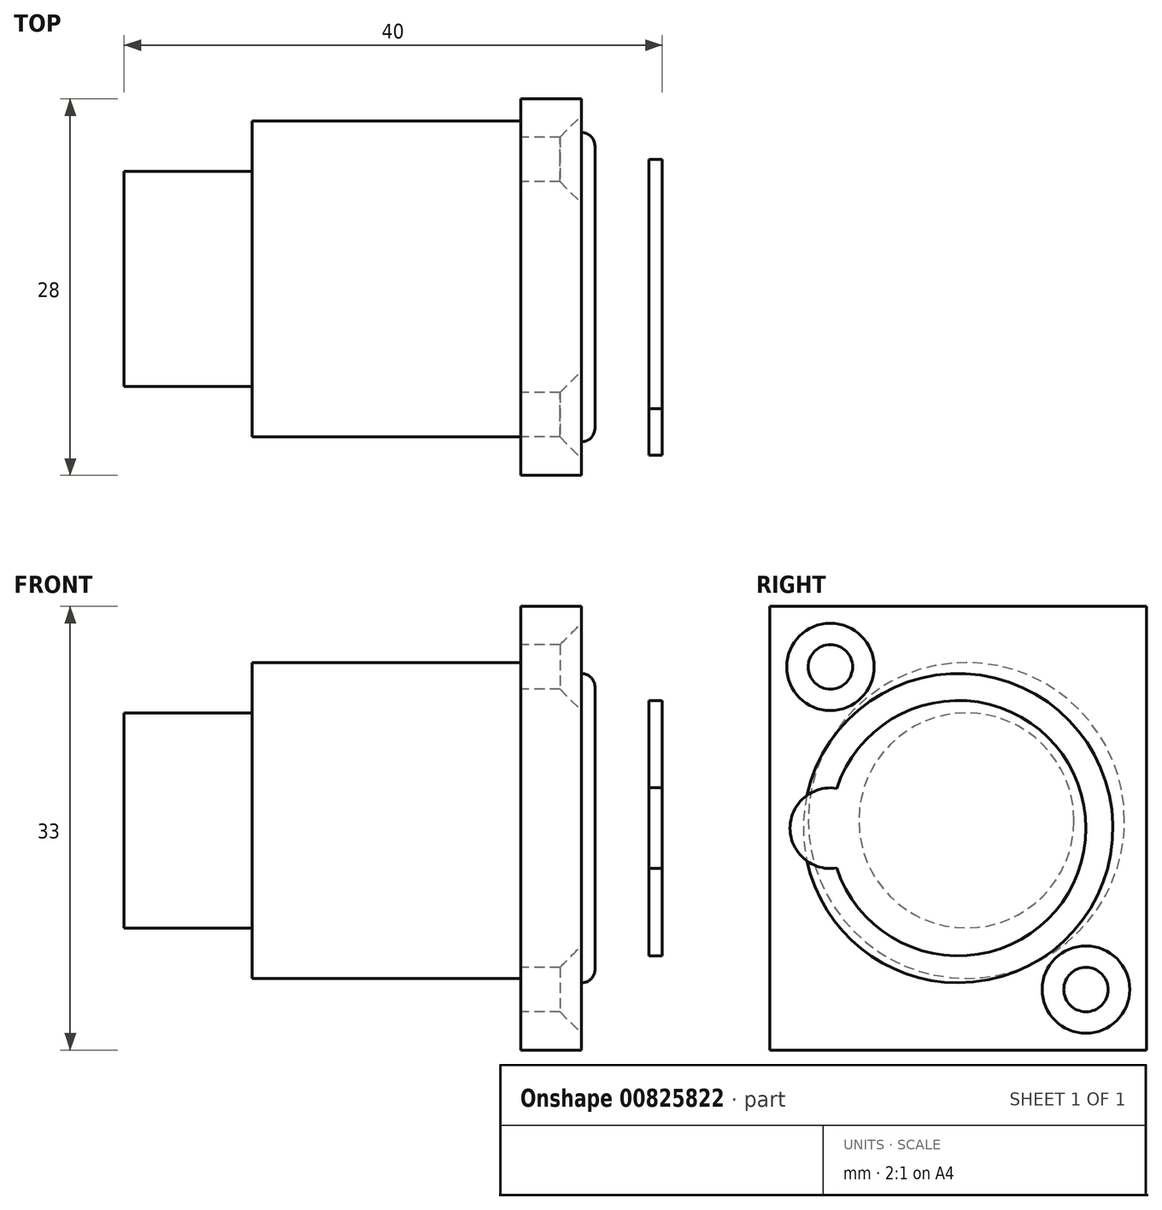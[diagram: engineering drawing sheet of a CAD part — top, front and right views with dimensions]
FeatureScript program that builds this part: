
annotation { "Feature Type Name" : "Feature", "Feature Type Description" : "" }
export const myFeature = defineFeature(function(context is Context, id is Id, definition is map)
    precondition{}
    {
        {
            var Q0;
            Q0=qCreatedBy(makeId("Right.planeOp"),FACE);
            var sketch = newSketch(context, id + "F0", { "sketchPlane" : qUnion([Q0])});
            skLineSegment(sketch, "E0.bottom", {"start": v(0, 0) * mm, "end": v(28, 0) * mm});
            skLineSegment(sketch, "E0.top", {"start": v(0, -33) * mm, "end": v(28, -33) * mm});
            skLineSegment(sketch, "E0.left", {"start": v(0, 0) * mm, "end": v(0, -33) * mm});
            skLineSegment(sketch, "E0.right", {"start": v(28, 0) * mm, "end": v(28, -33) * mm});
            skSolve(sketch);
        }
        {
            var Q0;
            Q0=makeQuery(id+"F0.imprint","IMPRINT",FACE,{"disambiguationData":[TD([[makeQuery(id+"F0.imprint","IMPRINT",EDGE,{"derivedFrom":sQuery(id+"F0.wireOp",EDGE,"E0.bottom")}),-1.0]])]});
            extrude(context, id + "F1", {"entities" : qUnion([Q0]), "depth" : 4.5 * mm, "offsetDistance" : 25 * mm});
        }
        {
            var Q0;
            Q0=makeQuery(id+"F1.opExtrude","CAP_FACE",FACE,{"disambiguationData":[OSD([sQuery(id+"F0.wireOp",EDGE,"E0.bottom"),sQuery(id+"F0.wireOp",EDGE,"E0.top"),sQuery(id+"F0.wireOp",EDGE,"E0.left"),sQuery(id+"F0.wireOp",EDGE,"E0.right")])],"isStart":true});
            var sketch = newSketch(context, id + "F2", { "sketchPlane" : qUnion([Q0])});
            skCircle(sketch, "E1", {"center": v(-14.61, -15.92) * mm, "radius": 11.75 * mm});
            skSolve(sketch);
        }
        {
            var Q0;
            Q0=makeQuery(id+"F2.imprint","IMPRINT",FACE,{"disambiguationData":[TD([[makeQuery(id+"F2.imprint","IMPRINT",EDGE,{"derivedFrom":sQuery(id+"F2.wireOp",EDGE,"E1")}),1.0]])]});
            extrude(context, id + "F3", {"entities" : qUnion([Q0]), "depth" : 20 * mm, "offsetDistance" : 25 * mm});
        }
        {
            var Q0;
            Q0=makeQuery(id+"F3.opExtrude","CAP_FACE",FACE,{"disambiguationData":[OSD([sQuery(id+"F2.wireOp",EDGE,"E1")])],"isStart":false});
            var sketch = newSketch(context, id + "F4", { "sketchPlane" : qUnion([Q0])});
            skCircle(sketch, "E2", {"center": v(-14.61, -15.92) * mm, "radius": 8 * mm});
            skSolve(sketch);
        }
        {
            var Q0;
            Q0=makeQuery(id+"F4.imprint","IMPRINT",FACE,{"disambiguationData":[TD([[makeQuery(id+"F4.imprint","IMPRINT",EDGE,{"derivedFrom":sQuery(id+"F4.wireOp",EDGE,"E2")}),1.0]])]});
            extrude(context, id + "F5", {"entities" : qUnion([Q0]), "operationType" : NewBodyOperationType.ADD, "depth" : 9.5 * mm, "offsetDistance" : 25 * mm});
        }
        {
            var Q0;
            Q0=makeQuery(id+"F1.opExtrude","CAP_FACE",FACE,{"disambiguationData":[OSD([sQuery(id+"F0.wireOp",EDGE,"E0.bottom"),sQuery(id+"F0.wireOp",EDGE,"E0.top"),sQuery(id+"F0.wireOp",EDGE,"E0.left"),sQuery(id+"F0.wireOp",EDGE,"E0.right")])],"isStart":false});
            var sketch = newSketch(context, id + "F6", { "sketchPlane" : qUnion([Q0])});
            skCircle(sketch, "E3", {"center": v(14, -16.5) * mm, "radius": 11.5 * mm});
            skPoint(sketch, "E4", {"position": v(14, 0) * mm});
            skPoint(sketch, "E5", {"position": v(0, -16.5) * mm});
            skSolve(sketch);
        }
        {
            var Q0;
            Q0=makeQuery(id+"F6.imprint","IMPRINT",FACE,{"disambiguationData":[TD([[makeQuery(id+"F6.imprint","IMPRINT",EDGE,{"derivedFrom":sQuery(id+"F6.wireOp",EDGE,"E3")}),1.0]])]});
            extrude(context, id + "F7", {"entities" : qUnion([Q0]), "operationType" : NewBodyOperationType.ADD, "depth" : 1 * mm, "offsetDistance" : 25 * mm});
        }
        {
            var Q0;
            Q0=makeQuery(id+"F7.opExtrude","CAP_FACE",FACE,{"disambiguationData":[OSD([sQuery(id+"F6.wireOp",EDGE,"E3")])],"isStart":false});
            fillet(context, id + "F8", {"entities" : qUnion([Q0]), "radius" : 1 * mm, "tangentPropagation" : true, "allowEdgeOverflow" : false});
        }
        {
            var Q0;
            Q0=makeQuery(id+"F7.opExtrude","CAP_FACE",FACE,{"disambiguationData":[OSD([sQuery(id+"F6.wireOp",EDGE,"E3")])],"isStart":false});
            var sketch = newSketch(context, id + "F9", { "sketchPlane" : qUnion([Q0])});
            skArc(sketch, "E6", {"start": v(4.97, -19.46) * mm, "mid": v(14, -26) * mm, "end": v(23.03, -19.46) * mm});
            skArc(sketch, "E7", {"start": v(4.97, -13.54) * mm, "mid": v(1.5, -16.5) * mm, "end": v(4.97, -19.46) * mm});
            skArc(sketch, "E8", {"start": v(23.03, -13.54) * mm, "mid": v(26.5, -16.5) * mm, "end": v(23.03, -19.46) * mm});
            skArc(sketch, "E9.trimOffspring", {"start": v(23.03, -13.54) * mm, "mid": v(14, -7) * mm, "end": v(4.97, -13.54) * mm});
            skArc(sketch, "E10", {"start": v(4.97, -13.54) * mm, "mid": v(4.5, -16.5) * mm, "end": v(4.97, -19.46) * mm});
            skArc(sketch, "E11", {"start": v(23.03, -13.54) * mm, "mid": v(23.5, -16.5) * mm, "end": v(23.03, -19.46) * mm});
            skSolve(sketch);
        }
        {
            var Q0;
            {var subQ6=sQuery(id+"F9.wireOp",EDGE,"E6");Q0=makeQuery(id+"F9.imprint","IMPRINT",FACE,{"disambiguationData":[TD([[makeQuery(id+"F9.imprint","IMPRINT",EDGE,{"derivedFrom":subQ6}),1.0]])]});}
            var Q1;
            {var subQ0=sQuery(id+"F9.wireOp",EDGE,"E7");var subQ1=sQuery(id+"F6.wireOp",EDGE,"E3");var subQ2=makeQuery(id+"F8.opFillet","BLEND_EDGE",EDGE,{"blendedFrom":[makeQuery(id+"F7.opExtrude","CAP_EDGE",EDGE,{"disambiguationData":[OSD([subQ1])],"isStart":false}),makeQuery(id+"F7.opExtrude","CAP_FACE",FACE,{"disambiguationData":[OSD([subQ1])],"isStart":false})],"blendedInto":[makeQuery(id+"F7.opExtrude","CAP_FACE",FACE,{"disambiguationData":[OSD([subQ1])],"isStart":false})]});var subQ3=makeQuery(id+"F9.imprint","INTERSECT",VERTEX,{"disambiguationData":[OD(0.0)],"derivedFrom":[subQ2,subQ0]});Q1=makeQuery(id+"F9.imprint","IMPRINT",FACE,{"disambiguationData":[TD([[makeQuery(id+"F9.imprint","IMPRINT",EDGE,{"disambiguationData":[TD([[subQ3,-1.0]])],"derivedFrom":subQ0}),1.0]])]});}
            var Q2;
            {var subQ0=sQuery(id+"F9.wireOp",EDGE,"E8");var subQ1=sQuery(id+"F6.wireOp",EDGE,"E3");var subQ2=makeQuery(id+"F8.opFillet","BLEND_EDGE",EDGE,{"blendedFrom":[makeQuery(id+"F7.opExtrude","CAP_EDGE",EDGE,{"disambiguationData":[OSD([subQ1])],"isStart":false}),makeQuery(id+"F7.opExtrude","CAP_FACE",FACE,{"disambiguationData":[OSD([subQ1])],"isStart":false})],"blendedInto":[makeQuery(id+"F7.opExtrude","CAP_FACE",FACE,{"disambiguationData":[OSD([subQ1])],"isStart":false})]});var subQ3=makeQuery(id+"F9.imprint","INTERSECT",VERTEX,{"disambiguationData":[OD(0.0)],"derivedFrom":[subQ2,subQ0]});Q2=makeQuery(id+"F9.imprint","IMPRINT",FACE,{"disambiguationData":[TD([[makeQuery(id+"F9.imprint","IMPRINT",EDGE,{"disambiguationData":[TD([[subQ3,-1.0]])],"derivedFrom":subQ0}),-1.0]])]});}
            var Q3;
            {var subQ0=sQuery(id+"F9.wireOp",EDGE,"E10");Q3=makeQuery(id+"F9.imprint","IMPRINT",FACE,{"disambiguationData":[TD([[makeQuery(id+"F9.imprint","IMPRINT",EDGE,{"derivedFrom":subQ0}),-1.0]])]});}
            var Q4;
            {var subQ0=sQuery(id+"F9.wireOp",EDGE,"E11");Q4=makeQuery(id+"F9.imprint","IMPRINT",FACE,{"disambiguationData":[TD([[makeQuery(id+"F9.imprint","IMPRINT",EDGE,{"derivedFrom":subQ0}),1.0]])]});}
            extrude(context, id + "F10", {"entities" : qUnion([Q0, Q1, Q2, Q3, Q4]), "depth" : 5 * mm, "offsetDistance" : 25 * mm});
        }
        {
            var Q0;
            {var subQ0=sQuery(id+"F9.wireOp",EDGE,"E10");Q0=makeQuery(id+"F9.imprint","IMPRINT",FACE,{"disambiguationData":[TD([[makeQuery(id+"F9.imprint","IMPRINT",EDGE,{"derivedFrom":subQ0}),-1.0]])]});}
            var Q1;
            {var subQ0=sQuery(id+"F9.wireOp",EDGE,"E7");var subQ1=sQuery(id+"F6.wireOp",EDGE,"E3");var subQ2=makeQuery(id+"F8.opFillet","BLEND_EDGE",EDGE,{"blendedFrom":[makeQuery(id+"F7.opExtrude","CAP_EDGE",EDGE,{"disambiguationData":[OSD([subQ1])],"isStart":false}),makeQuery(id+"F7.opExtrude","CAP_FACE",FACE,{"disambiguationData":[OSD([subQ1])],"isStart":false})],"blendedInto":[makeQuery(id+"F7.opExtrude","CAP_FACE",FACE,{"disambiguationData":[OSD([subQ1])],"isStart":false})]});var subQ3=makeQuery(id+"F9.imprint","INTERSECT",VERTEX,{"disambiguationData":[OD(0.0)],"derivedFrom":[subQ2,subQ0]});Q1=makeQuery(id+"F9.imprint","IMPRINT",FACE,{"disambiguationData":[TD([[makeQuery(id+"F9.imprint","IMPRINT",EDGE,{"disambiguationData":[TD([[subQ3,-1.0]])],"derivedFrom":subQ0}),1.0]])]});}
            var Q2;
            {var subQ0=sQuery(id+"F9.wireOp",EDGE,"E11");Q2=makeQuery(id+"F9.imprint","IMPRINT",FACE,{"disambiguationData":[TD([[makeQuery(id+"F9.imprint","IMPRINT",EDGE,{"derivedFrom":subQ0}),1.0]])]});}
            var Q3;
            {var subQ0=sQuery(id+"F9.wireOp",EDGE,"E8");var subQ1=sQuery(id+"F6.wireOp",EDGE,"E3");var subQ2=makeQuery(id+"F8.opFillet","BLEND_EDGE",EDGE,{"blendedFrom":[makeQuery(id+"F7.opExtrude","CAP_EDGE",EDGE,{"disambiguationData":[OSD([subQ1])],"isStart":false}),makeQuery(id+"F7.opExtrude","CAP_FACE",FACE,{"disambiguationData":[OSD([subQ1])],"isStart":false})],"blendedInto":[makeQuery(id+"F7.opExtrude","CAP_FACE",FACE,{"disambiguationData":[OSD([subQ1])],"isStart":false})]});var subQ3=makeQuery(id+"F9.imprint","INTERSECT",VERTEX,{"disambiguationData":[OD(0.0)],"derivedFrom":[subQ2,subQ0]});Q3=makeQuery(id+"F9.imprint","IMPRINT",FACE,{"disambiguationData":[TD([[makeQuery(id+"F9.imprint","IMPRINT",EDGE,{"disambiguationData":[TD([[subQ3,-1.0]])],"derivedFrom":subQ0}),-1.0]])]});}
            extrude(context, id + "F11", {"entities" : qUnion([Q0, Q1, Q2, Q3]), "operationType" : NewBodyOperationType.REMOVE, "depth" : 4 * mm, "offsetDistance" : 25 * mm});
        }
        {
            var Q0;
            Q0=makeQuery(id+"F1.opExtrude","CAP_FACE",FACE,{"disambiguationData":[OSD([sQuery(id+"F0.wireOp",EDGE,"E0.bottom"),sQuery(id+"F0.wireOp",EDGE,"E0.top"),sQuery(id+"F0.wireOp",EDGE,"E0.left"),sQuery(id+"F0.wireOp",EDGE,"E0.right")])],"isStart":false});
            var sketch = newSketch(context, id + "F12", { "sketchPlane" : qUnion([Q0])});
            skCircle(sketch, "E12", {"center": v(4.5, -4.5) * mm, "radius": 1.65 * mm});
            skCircle(sketch, "E13", {"center": v(23.5, -28.5) * mm, "radius": 1.65 * mm});
            skCircle(sketch, "E14", {"center": v(23.5, -4.5) * mm, "radius": 1.65 * mm});
            skCircle(sketch, "E15", {"center": v(4.5, -28.5) * mm, "radius": 1.65 * mm});
            skLineSegment(sketch, "E16", {"start": v(23.5, -4.5) * mm, "end": v(4.5, -4.5) * mm});
            skLineSegment(sketch, "E17", {"start": v(23.5, -4.5) * mm, "end": v(23.5, -28.5) * mm});
            skPoint(sketch, "E18", {"position": v(14, -4.5) * mm});
            skPoint(sketch, "E19", {"position": v(14, 0) * mm});
            skPoint(sketch, "E20", {"position": v(28, -16.5) * mm});
            skPoint(sketch, "E21", {"position": v(23.5, -16.5) * mm});
            skSolve(sketch);
        }
        {
            var Q0;
            Q0=sQuery(id+"F12.wireOp",VERTEX,"E16.end");
            var Q1;
            Q1=makeQuery(id+"F1.opExtrude","SWEPT_BODY",BODY,{"disambiguationData":[OSD([sQuery(id+"F0.wireOp",EDGE,"E0.bottom"),sQuery(id+"F0.wireOp",EDGE,"E0.top"),sQuery(id+"F0.wireOp",EDGE,"E0.left"),sQuery(id+"F0.wireOp",EDGE,"E0.right")])]});
            hole(context, id + "F13", {"style" : HoleStyle.C_SINK, "endStyle" : HoleEndStyle.THROUGH, "holeDiameter" : 3.3 * mm, "cSinkDiameter" : 6.5 * mm, "cSinkAngle" : 90 * degree, "majorDiameter" : 5 * mm, "isTappedThrough" : true, "tappedDepth" : 12 * mm, "tapClearance" : 3, "locations" : qUnion([Q0]), "scope" : qUnion([Q1]), "startStyle" : HoleStartStyle.PART});
        }
        {
            var Q0;
            Q0=sQuery(id+"F12.wireOp",VERTEX,"E17.end");
            var Q1;
            Q1=makeQuery(id+"F1.opExtrude","SWEPT_BODY",BODY,{"disambiguationData":[OSD([sQuery(id+"F0.wireOp",EDGE,"E0.bottom"),sQuery(id+"F0.wireOp",EDGE,"E0.top"),sQuery(id+"F0.wireOp",EDGE,"E0.left"),sQuery(id+"F0.wireOp",EDGE,"E0.right")])]});
            hole(context, id + "F14", {"style" : HoleStyle.C_SINK, "endStyle" : HoleEndStyle.THROUGH, "holeDiameter" : 3.3 * mm, "cSinkDiameter" : 6.5 * mm, "cSinkAngle" : 90 * degree, "majorDiameter" : 5 * mm, "isTappedThrough" : true, "tappedDepth" : 12 * mm, "tapClearance" : 3, "locations" : qUnion([Q0]), "scope" : qUnion([Q1]), "startStyle" : HoleStartStyle.PART});
        }
    });
